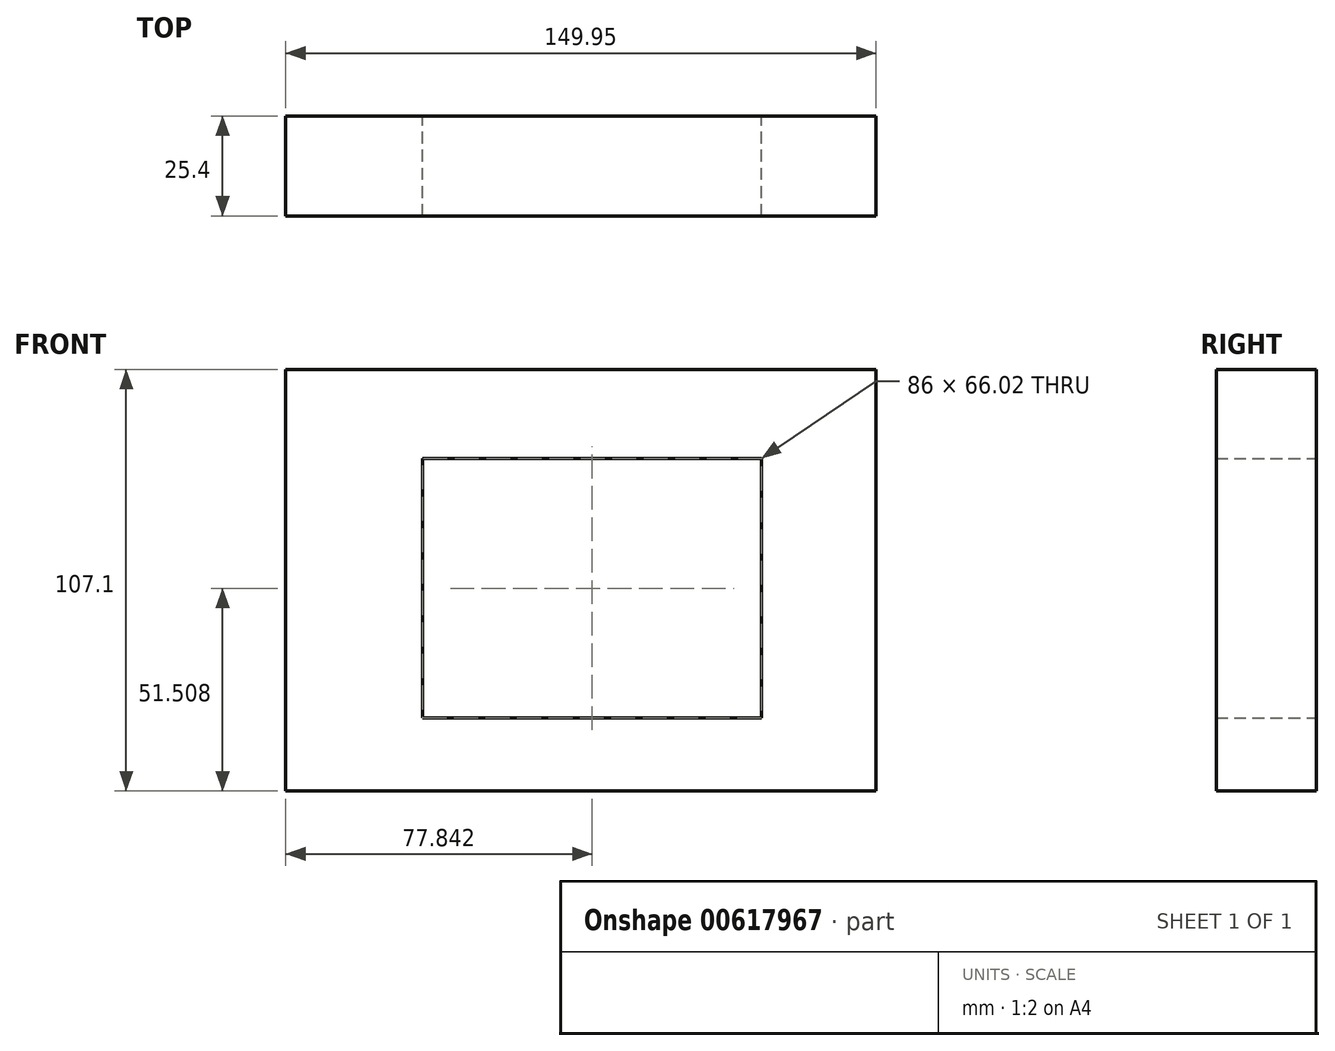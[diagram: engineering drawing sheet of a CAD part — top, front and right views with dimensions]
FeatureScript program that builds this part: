
annotation { "Feature Type Name" : "Feature", "Feature Type Description" : "" }
export const myFeature = defineFeature(function(context is Context, id is Id, definition is map)
    precondition{}
    {
        {
            var Q0;
            Q0=qCreatedBy(makeId("Front.planeOp"),FACE);
            var sketch = newSketch(context, id + "F0", { "sketchPlane" : qUnion([Q0])});
            skLineSegment(sketch, "E0.bottom", {"start": v(-55.57, 61.58) * mm, "end": v(94.38, 61.58) * mm});
            skLineSegment(sketch, "E0.top", {"start": v(-55.57, -45.52) * mm, "end": v(94.38, -45.52) * mm});
            skLineSegment(sketch, "E0.left", {"start": v(-55.57, 61.58) * mm, "end": v(-55.57, -45.52) * mm});
            skLineSegment(sketch, "E0.right", {"start": v(94.38, 61.58) * mm, "end": v(94.38, -45.52) * mm});
            skLineSegment(sketch, "E1.bottom", {"start": v(-20.73, 39) * mm, "end": v(65.27, 39) * mm});
            skLineSegment(sketch, "E1.top", {"start": v(-20.73, -27.02) * mm, "end": v(65.27, -27.02) * mm});
            skLineSegment(sketch, "E1.left", {"start": v(-20.73, 39) * mm, "end": v(-20.73, -27.02) * mm});
            skLineSegment(sketch, "E1.right", {"start": v(65.27, 39) * mm, "end": v(65.27, -27.02) * mm});
            skSolve(sketch);
        }
        {
            var Q0;
            Q0 = qSketchRegion(id + "F0", true);
            extrude(context, id + "F1", {"entities" : qUnion([Q0]), "depth" : 25.4 * mm, "offsetDistance" : 25.4 * mm});
        }
    });
